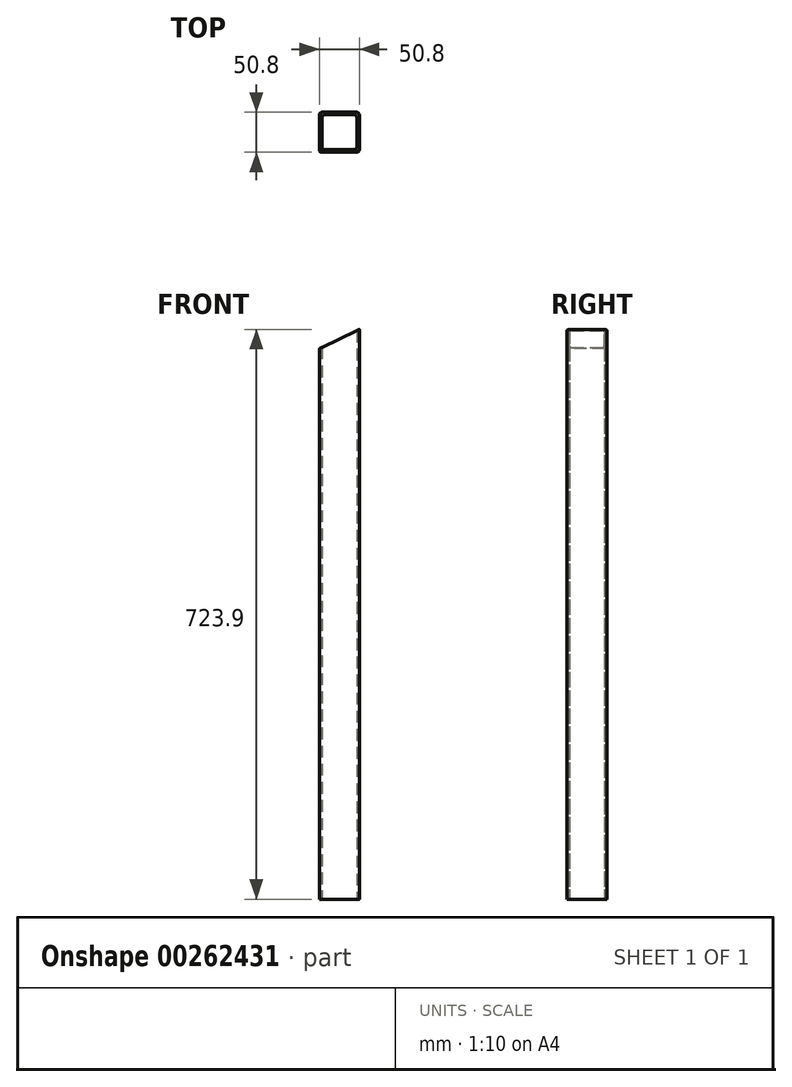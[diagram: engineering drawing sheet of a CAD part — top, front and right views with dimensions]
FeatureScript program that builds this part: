
annotation { "Feature Type Name" : "Feature", "Feature Type Description" : "" }
export const myFeature = defineFeature(function(context is Context, id is Id, definition is map)
    precondition{}
    {
        {
            var Q0;
            Q0=qCreatedBy(makeId("Top.planeOp"),FACE);
            var sketch = newSketch(context, id + "F0", { "sketchPlane" : qUnion([Q0])});
            skLineSegment(sketch, "E0.bottom", {"start": v(19.05, 22.23) * mm, "end": v(-19.05, 22.23) * mm});
            skLineSegment(sketch, "E0.top", {"start": v(19.05, -22.23) * mm, "end": v(-19.05, -22.23) * mm});
            skLineSegment(sketch, "E0.left", {"start": v(22.23, 19.05) * mm, "end": v(22.23, -19.05) * mm});
            skLineSegment(sketch, "E0.right", {"start": v(-22.23, 19.05) * mm, "end": v(-22.23, -19.05) * mm});
            skPoint(sketch, "E0.middle", {"position": v(0, 0) * mm});
            skLineSegment(sketch, "E1.bottom", {"start": v(22.23, 25.4) * mm, "end": v(-22.23, 25.4) * mm});
            skLineSegment(sketch, "E1.top", {"start": v(22.23, -25.4) * mm, "end": v(-22.23, -25.4) * mm});
            skLineSegment(sketch, "E1.left", {"start": v(25.4, 22.22) * mm, "end": v(25.4, -22.22) * mm});
            skLineSegment(sketch, "E1.right", {"start": v(-25.4, 22.22) * mm, "end": v(-25.4, -22.22) * mm});
            skPoint(sketch, "E2.visualSharp", {"position": v(-25.4, 25.4) * mm});
            skArc(sketch, "E2.filletArc", {"start": v(-22.23, 25.4) * mm, "mid": v(-24.47, 24.47) * mm, "end": v(-25.4, 22.22) * mm});
            skPoint(sketch, "E3.visualSharp", {"position": v(-22.23, 22.23) * mm});
            skArc(sketch, "E3.filletArc", {"start": v(-19.05, 22.23) * mm, "mid": v(-21.3, 21.3) * mm, "end": v(-22.23, 19.05) * mm});
            skPoint(sketch, "E4.visualSharp", {"position": v(25.4, 25.4) * mm});
            skArc(sketch, "E4.filletArc", {"start": v(25.4, 22.22) * mm, "mid": v(24.47, 24.47) * mm, "end": v(22.23, 25.4) * mm});
            skPoint(sketch, "E5.visualSharp", {"position": v(22.23, 22.23) * mm});
            skArc(sketch, "E5.filletArc", {"start": v(22.23, 19.05) * mm, "mid": v(21.3, 21.3) * mm, "end": v(19.05, 22.23) * mm});
            skPoint(sketch, "E6.visualSharp", {"position": v(-25.4, -25.4) * mm});
            skArc(sketch, "E6.filletArc", {"start": v(-25.4, -22.22) * mm, "mid": v(-24.47, -24.47) * mm, "end": v(-22.23, -25.4) * mm});
            skPoint(sketch, "E7.visualSharp", {"position": v(-22.23, -22.23) * mm});
            skArc(sketch, "E7.filletArc", {"start": v(-22.23, -19.05) * mm, "mid": v(-21.3, -21.3) * mm, "end": v(-19.05, -22.23) * mm});
            skPoint(sketch, "E8.visualSharp", {"position": v(22.23, -22.23) * mm});
            skArc(sketch, "E8.filletArc", {"start": v(19.05, -22.23) * mm, "mid": v(21.3, -21.3) * mm, "end": v(22.23, -19.05) * mm});
            skPoint(sketch, "E9.visualSharp", {"position": v(25.4, -25.4) * mm});
            skArc(sketch, "E9.filletArc", {"start": v(22.23, -25.4) * mm, "mid": v(24.47, -24.47) * mm, "end": v(25.4, -22.22) * mm});
            skSolve(sketch);
        }
        {
            var Q0;
            Q0 = qSketchRegion(id + "F0", true);
            extrude(context, id + "F1", {"entities" : qUnion([Q0]), "depth" : 723.9 * mm});
        }
        {
            var Q0;
            Q0=qCreatedBy(makeId("Front.planeOp"),FACE);
            var sketch = newSketch(context, id + "F2", { "sketchPlane" : qUnion([Q0])});
            skLineSegment(sketch, "E10.bottom", {"start": v(25.4, 723.9) * mm, "end": v(-25.4, 723.9) * mm});
            skLineSegment(sketch, "E10.right", {"start": v(-25.4, 723.9) * mm, "end": v(-25.4, 699.48) * mm});
            skPoint(sketch, "E10.middle", {"position": v(0, 711.7) * mm});
            skLineSegment(sketch, "E11", {"start": v(-25.4, 699.48) * mm, "end": v(25.4, 723.9) * mm});
            skPoint(sketch, "E10.left.end.orphan", {"position": v(25.4, 699.48) * mm});
            skSolve(sketch);
        }
        {
            var Q0;
            Q0 = qSketchRegion(id + "F2", true);
            extrude(context, id + "F3", {"entities" : qUnion([Q0]), "operationType" : NewBodyOperationType.REMOVE, "oppositeDirection" : true, "depth" : 50.8 * mm, "hasSecondDirection" : true, "secondDirectionOppositeDirection" : false, "secondDirectionDepth" : 50.8 * mm});
        }
    });
